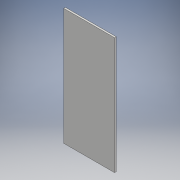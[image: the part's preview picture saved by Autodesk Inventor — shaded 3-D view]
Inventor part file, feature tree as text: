
AUTODESK INVENTOR PART (.ipt)
format: ipt  version: 2018 (Build 220112000, 112)  size: 90,624 bytes
history: native  units: mm
features: extrude x1, sketch x1
ambient origin geometry x8: Origin, YZ Plane, XZ Plane, XY Plane, X Axis, Y Axis, Z Axis, Center Point
bodies: Solid1 (feature_tree)
feature tree (2):
  extrude  "Extrusion1"  Depth=108.0mm
  sketch  "Sketch1"  dims[d0=47.0mm d1=108.0mm d2=1.6mm d3=0.0mm]
